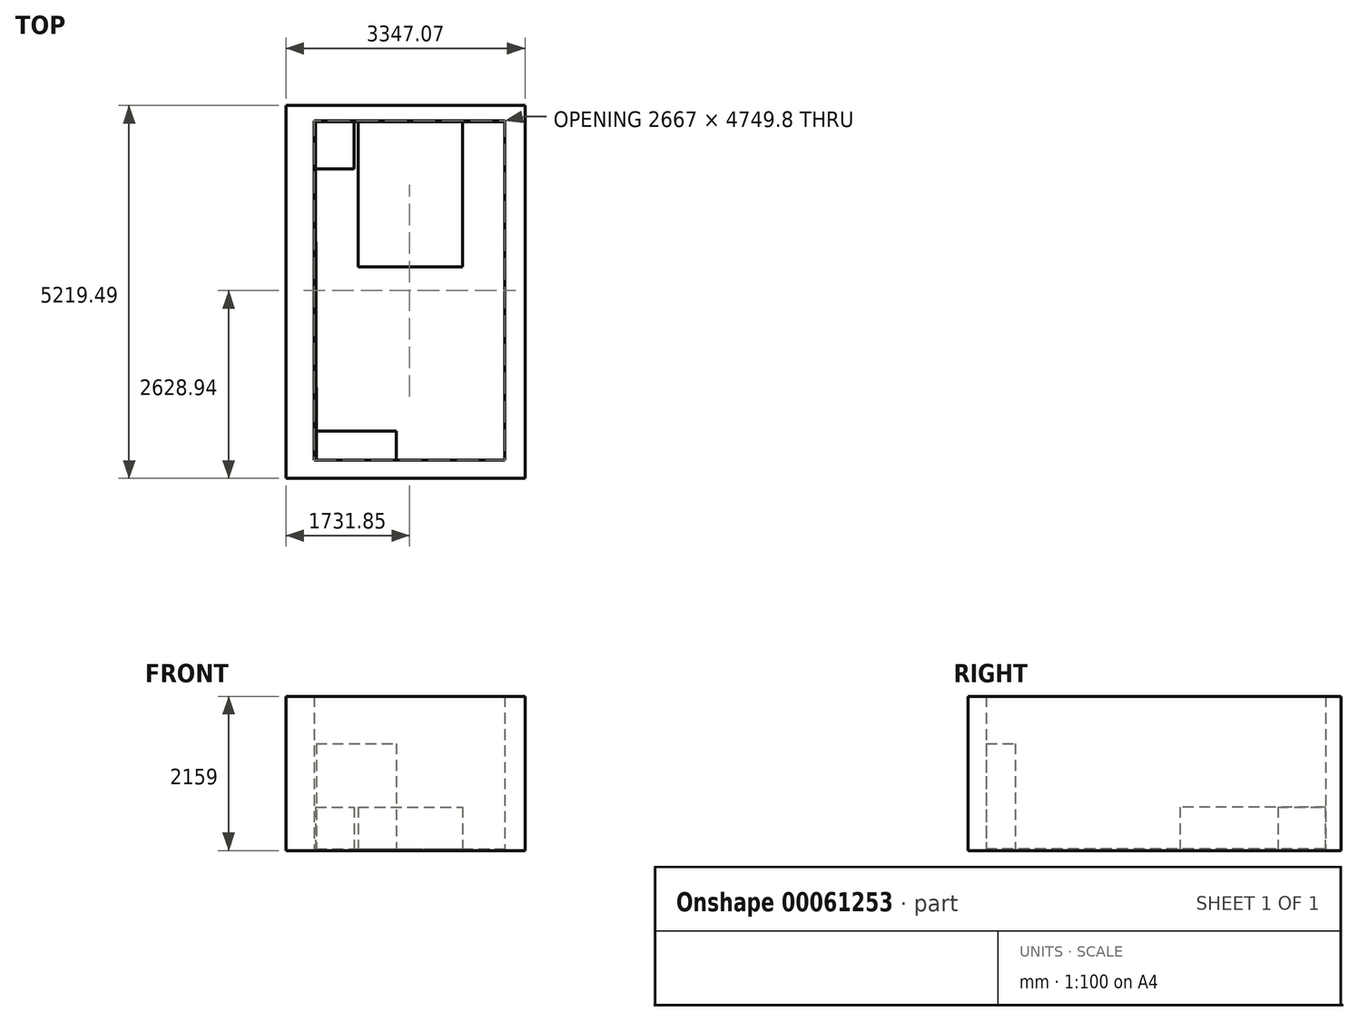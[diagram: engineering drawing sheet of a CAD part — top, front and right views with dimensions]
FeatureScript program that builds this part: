
annotation { "Feature Type Name" : "Feature", "Feature Type Description" : "" }
export const myFeature = defineFeature(function(context is Context, id is Id, definition is map)
    precondition{}
    {
        {
            var Q0;
            Q0=qCreatedBy(makeId("Top.planeOp"),FACE);
            var sketch = newSketch(context, id + "F0", { "sketchPlane" : qUnion([Q0])});
            skLineSegment(sketch, "E0.top", {"start": v(-1104.9, -1259.39) * mm, "end": v(1562.1, -1259.39) * mm});
            skLineSegment(sketch, "E0.left", {"start": v(-1104.9, 3490.41) * mm, "end": v(-1104.9, -1259.39) * mm});
            skLineSegment(sketch, "E0.right", {"start": v(1562.1, 3490.41) * mm, "end": v(1562.1, -1259.39) * mm});
            skLineSegment(sketch, "E1", {"start": v(-1104.9, 3490.41) * mm, "end": v(1562.1, 3490.41) * mm});
            skLineSegment(sketch, "E2", {"start": v(-1503.24, 3706.06) * mm, "end": v(1843.83, 3706.06) * mm});
            skLineSegment(sketch, "E3", {"start": v(1843.83, 3706.06) * mm, "end": v(1843.83, -1513.43) * mm});
            skLineSegment(sketch, "E4", {"start": v(1843.83, -1513.43) * mm, "end": v(-1503.24, -1513.43) * mm});
            skLineSegment(sketch, "E5", {"start": v(-1503.24, -1513.43) * mm, "end": v(-1503.24, 3706.06) * mm});
            skSolve(sketch);
        }
        {
            var Q0;
            Q0=makeQuery(id+"F0.imprint","IMPRINT",FACE,{"disambiguationData":[TD([[makeQuery(id+"F0.imprint","IMPRINT",EDGE,{"derivedFrom":sQuery(id+"F0.wireOp",EDGE,"E0.top")}),-1.0]])]});
            extrude(context, id + "F1", {"entities" : qUnion([Q0]), "depth" : 2133.6 * mm});
        }
        {
            var Q0;
            Q0=qCreatedBy(makeId("Top.planeOp"),FACE);
            var sketch = newSketch(context, id + "F2", { "sketchPlane" : qUnion([Q0])});
            skLineSegment(sketch, "E6.bottom", {"start": v(-1086.5, 3490.41) * mm, "end": v(1558.96, 3490.41) * mm});
            skLineSegment(sketch, "E6.top", {"start": v(-1086.5, -1264.82) * mm, "end": v(1558.96, -1264.82) * mm});
            skLineSegment(sketch, "E6.left", {"start": v(-1086.5, 3490.41) * mm, "end": v(-1086.5, -1264.82) * mm});
            skLineSegment(sketch, "E6.right", {"start": v(1558.96, 3490.41) * mm, "end": v(1558.96, -1264.82) * mm});
            skSolve(sketch);
        }
        {
            var Q0;
            Q0=makeQuery(id+"F2.imprint","IMPRINT",FACE,{"disambiguationData":[TD([[makeQuery(id+"F2.imprint","IMPRINT",EDGE,{"derivedFrom":sQuery(id+"F2.wireOp",EDGE,"E6.bottom")}),-1.0]])]});
            extrude(context, id + "F3", {"entities" : qUnion([Q0]), "operationType" : NewBodyOperationType.REMOVE, "oppositeDirection" : true, "depth" : 25.4 * mm});
        }
        {
            var Q0;
            Q0=makeQuery(id+"F1.opExtrude","CAP_FACE",FACE,{"disambiguationData":[OSD([sQuery(id+"F0.wireOp",EDGE,"E0.top"),sQuery(id+"F0.wireOp",EDGE,"E0.left"),sQuery(id+"F0.wireOp",EDGE,"E0.right"),sQuery(id+"F0.wireOp",EDGE,"E1"),sQuery(id+"F0.wireOp",EDGE,"E2"),sQuery(id+"F0.wireOp",EDGE,"E3"),sQuery(id+"F0.wireOp",EDGE,"E4"),sQuery(id+"F0.wireOp",EDGE,"E5")])],"isStart":false});
            extrude(context, id + "F4", {"entities" : qUnion([Q0]), "operationType" : NewBodyOperationType.ADD, "depth" : 25.4 * mm});
        }
        {
            var Q0;
            Q0=qCreatedBy(makeId("Top.planeOp"),FACE);
            var sketch = newSketch(context, id + "F5", { "sketchPlane" : qUnion([Q0])});
            skLineSegment(sketch, "E7", {"start": v(-1086.5, 3482.17) * mm, "end": v(1567.2, 3482.17) * mm});
            skLineSegment(sketch, "E8", {"start": v(1567.2, 3482.17) * mm, "end": v(1567.2, -1264.82) * mm});
            skLineSegment(sketch, "E9", {"start": v(1567.2, -1264.82) * mm, "end": v(-1078.26, -1264.82) * mm});
            skLineSegment(sketch, "E10", {"start": v(-1078.26, -1264.82) * mm, "end": v(-1086.5, 3482.17) * mm});
            skSolve(sketch);
        }
        {
            var Q0;
            Q0=makeQuery(id+"F5.imprint","IMPRINT",FACE,{"disambiguationData":[TD([[makeQuery(id+"F5.imprint","IMPRINT",EDGE,{"derivedFrom":sQuery(id+"F5.wireOp",EDGE,"E7")}),-1.0]])]});
            extrude(context, id + "F6", {"entities" : qUnion([Q0]), "operationType" : NewBodyOperationType.ADD, "depth" : 25.4 * mm});
        }
        {
            var Q0;
            Q0=makeQuery(id+"F6.opExtrude","CAP_FACE",FACE,{"disambiguationData":[OSD([sQuery(id+"F5.wireOp",EDGE,"E7"),sQuery(id+"F5.wireOp",EDGE,"E8"),sQuery(id+"F5.wireOp",EDGE,"E9"),sQuery(id+"F5.wireOp",EDGE,"E10")])],"isStart":false});
            var sketch = newSketch(context, id + "F7", { "sketchPlane" : qUnion([Q0])});
            skLineSegment(sketch, "E11.bottom", {"start": v(-492.45, 3482.17) * mm, "end": v(968.05, 3482.17) * mm});
            skLineSegment(sketch, "E11.top", {"start": v(-492.45, 1450.17) * mm, "end": v(968.05, 1450.17) * mm});
            skLineSegment(sketch, "E11.left", {"start": v(-492.45, 3482.17) * mm, "end": v(-492.45, 1450.17) * mm});
            skLineSegment(sketch, "E11.right", {"start": v(968.05, 3482.17) * mm, "end": v(968.05, 1450.17) * mm});
            skSolve(sketch);
        }
        {
            var Q0;
            Q0=makeQuery(id+"F7.imprint","IMPRINT",FACE,{"disambiguationData":[TD([[makeQuery(id+"F7.imprint","IMPRINT",EDGE,{"derivedFrom":sQuery(id+"F7.wireOp",EDGE,"E11.bottom")}),-1.0]])]});
            extrude(context, id + "F8", {"entities" : qUnion([Q0]), "operationType" : NewBodyOperationType.ADD, "depth" : 584.2 * mm});
        }
        {
            var Q0;
            Q0=makeQuery(id+"F6.opExtrude","CAP_FACE",FACE,{"disambiguationData":[OSD([sQuery(id+"F5.wireOp",EDGE,"E7"),sQuery(id+"F5.wireOp",EDGE,"E8"),sQuery(id+"F5.wireOp",EDGE,"E9"),sQuery(id+"F5.wireOp",EDGE,"E10")])],"isStart":false});
            var sketch = newSketch(context, id + "F9", { "sketchPlane" : qUnion([Q0])});
            skLineSegment(sketch, "E12.bottom", {"start": v(-1086.5, 3482.17) * mm, "end": v(-546.75, 3482.17) * mm});
            skLineSegment(sketch, "E12.top", {"start": v(-1086.5, 2821.77) * mm, "end": v(-546.75, 2821.77) * mm});
            skLineSegment(sketch, "E12.left", {"start": v(-1086.5, 3482.17) * mm, "end": v(-1086.5, 2821.77) * mm});
            skLineSegment(sketch, "E12.right", {"start": v(-546.75, 3482.17) * mm, "end": v(-546.75, 2821.77) * mm});
            skSolve(sketch);
        }
        {
            var Q0;
            {var subQ0=sQuery(id+"F9.wireOp",EDGE,"E12.bottom");Q0=makeQuery(id+"F9.imprint","IMPRINT",FACE,{"disambiguationData":[TD([[makeQuery(id+"F9.imprint","IMPRINT",EDGE,{"derivedFrom":subQ0}),-1.0]])]});}
            extrude(context, id + "F10", {"entities" : qUnion([Q0]), "operationType" : NewBodyOperationType.ADD, "depth" : 584.2 * mm});
        }
        {
            var Q0;
            Q0=makeQuery(id+"F6.opExtrude","CAP_FACE",FACE,{"disambiguationData":[OSD([sQuery(id+"F5.wireOp",EDGE,"E7"),sQuery(id+"F5.wireOp",EDGE,"E8"),sQuery(id+"F5.wireOp",EDGE,"E9"),sQuery(id+"F5.wireOp",EDGE,"E10")])],"isStart":false});
            var sketch = newSketch(context, id + "F11", { "sketchPlane" : qUnion([Q0])});
            skLineSegment(sketch, "E13.bottom", {"start": v(-1078.27, -1259.39) * mm, "end": v(39.33, -1259.39) * mm});
            skLineSegment(sketch, "E13.top", {"start": v(-1078.27, -852.99) * mm, "end": v(39.33, -852.99) * mm});
            skLineSegment(sketch, "E13.left", {"start": v(-1078.27, -1259.39) * mm, "end": v(-1078.27, -852.99) * mm});
            skLineSegment(sketch, "E13.right", {"start": v(39.33, -1259.39) * mm, "end": v(39.33, -852.99) * mm});
            skSolve(sketch);
        }
        {
            var Q0;
            Q0=makeQuery(id+"F11.imprint","IMPRINT",FACE,{"disambiguationData":[TD([[makeQuery(id+"F11.imprint","IMPRINT",EDGE,{"derivedFrom":sQuery(id+"F11.wireOp",EDGE,"E13.bottom")}),1.0]])]});
            extrude(context, id + "F12", {"entities" : qUnion([Q0]), "operationType" : NewBodyOperationType.ADD, "depth" : 1473.2 * mm});
        }
    });
